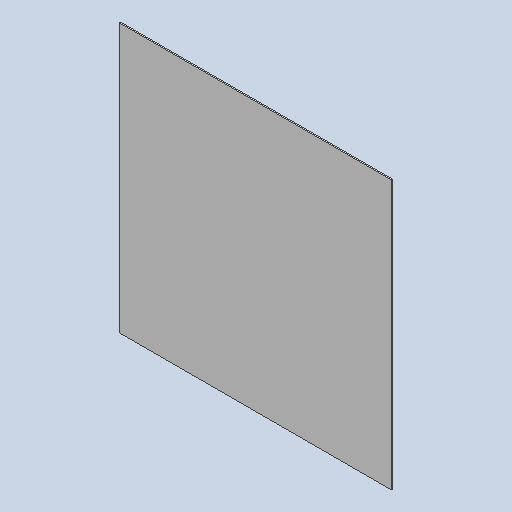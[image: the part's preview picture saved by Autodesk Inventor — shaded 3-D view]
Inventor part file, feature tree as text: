
AUTODESK INVENTOR PART (.ipt)
format: ipt  version: 2025 (Build 290162010, 162A)  size: 108,032 bytes
history: native  units: mm
features: extrude x1, other x1
ambient origin geometry x8: Origin, YZ Plane, XZ Plane, XY Plane, X Axis, Y Axis, Z Axis, Center Point
bodies: Solid1 (feature_tree)
feature tree (2):
  extrude  "Extrusion1"  Depth=2180.0mm
  other  "Definition1"
